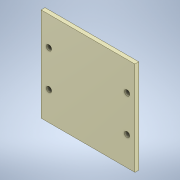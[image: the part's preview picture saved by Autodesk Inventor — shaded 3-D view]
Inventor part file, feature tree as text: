
AUTODESK INVENTOR PART (.ipt)
format: ipt  version: 2020 (Build 240168000, 168)  size: 105,984 bytes
history: native  units: in
note: dims shown in document units (in); Inventor stores cm internally (conversion verified against a paired STEP export)
features: sketch x2, extrude x1, hole x1
ambient origin geometry x8: Origin, YZ Plane, XZ Plane, XY Plane, X Axis, Y Axis, Z Axis, Center Point
bodies: Solid1 (feature_tree)
feature tree (4):
  extrude  "Extrusion1"  Depth=6.0in
  hole  "Hole1"  [1 undecoded]
  sketch  "Sketch1"  dims[d0=6.0in d1=6.0in]
  sketch  "Sketch2"  dims[d2=0.25in d3=0.0in d4=5.0in d5=2.3125in d6=0.344in d7=0.75in d8=0.635in d9=0.25in d10=0.5635in d11=1.0in d12=0.8108in]
note: 1 required parameter value undecoded (feature->parameter linkage not recoverable at this tier; creation-order binding heuristic only, values carry confidence <= 0.55)
